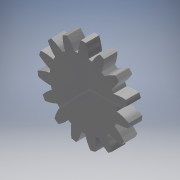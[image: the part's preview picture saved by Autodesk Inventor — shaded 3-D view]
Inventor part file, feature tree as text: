
AUTODESK INVENTOR PART (.ipt)
format: ipt  version: 2017 (Build 210142000, 142)  size: 202,240 bytes
history: native  units: mm (DEFAULTED — no unit token found)
features: plane x3, other x3, sketch x2, extrude x1
ambient origin geometry x8: Origin, YZ Plane, XZ Plane, XY Plane, X Axis, Y Axis, Z Axis, Center Point
bodies: Solid1 (feature_tree)
feature tree (9):
  extrude  "Extrusion1"  Depth=6.35mm TaperAngle=0.0deg
  plane  "Work Plane1"
  plane  "Work Plane2"
  plane  "Work Plane3"
  other  "Spur Gear"
  sketch  "Sketch1"  dims[d0=43.18mm d1=6.35mm d2=0.0mm]
  sketch  "Sketch2"  dims[d3=38.1mm d4=76.2mm d5=0.0mm d6=0.0mm d7=2.094395mm d9=0.0mm d14=0.0mm d15=173.99mm d16=0.0mm d17=0.0mm d18=0.0mm d19=173.99mm]
  other  "Srf1"
  other  "Pitch Diameter"
